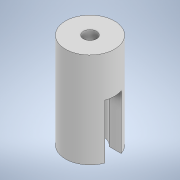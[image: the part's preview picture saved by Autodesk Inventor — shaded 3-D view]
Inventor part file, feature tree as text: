
AUTODESK INVENTOR PART (.ipt)
format: ipt  version: 2022.4 (Build 264492010, 492A)  size: 126,464 bytes
history: native  units: mm
features: sketch x2, revolve x1, extrude x1
ambient origin geometry x8: Origin, YZ Plane, XZ Plane, XY Plane, X Axis, Y Axis, Z Axis, Center Point
bodies: Solid1 (feature_tree)
feature tree (4):
  revolve  "Revolution1"  [1 undecoded]
  extrude  "Extrusion1"  Depth=10.0mm
  sketch  "Sketch1"  dims[d0=9.0mm d1=35.0mm]
  sketch  "Sketch2"  dims[d2=17.5mm d3=10.0mm d4=2.45mm d5=5.0mm d6=90.0deg d7=2.0mm d8=2.0mm d9=0.0mm d10=0.0mm d11=5.0mm]
note: 1 required parameter value undecoded (feature->parameter linkage not recoverable at this tier; creation-order binding heuristic only, values carry confidence <= 0.55)
